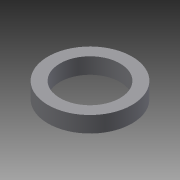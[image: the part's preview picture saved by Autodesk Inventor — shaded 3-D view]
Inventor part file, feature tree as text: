
AUTODESK INVENTOR PART (.ipt)
format: ipt  version: 2013 (Build 170138000, 138)  size: 73,216 bytes
history: native  units: mm
features: extrude x1, sketch x1
ambient origin geometry x8: Origin, YZ Plane, XZ Plane, XY Plane, X Axis, Y Axis, Z Axis, Center Point
bodies: Solid1 (feature_tree)
feature tree (2):
  extrude  "Extrusion1"  Depth=21.0mm
  sketch  "Sketch1"  dims[d0=15.0mm d2=21.0mm d3=4.0mm d4=0.0mm]
